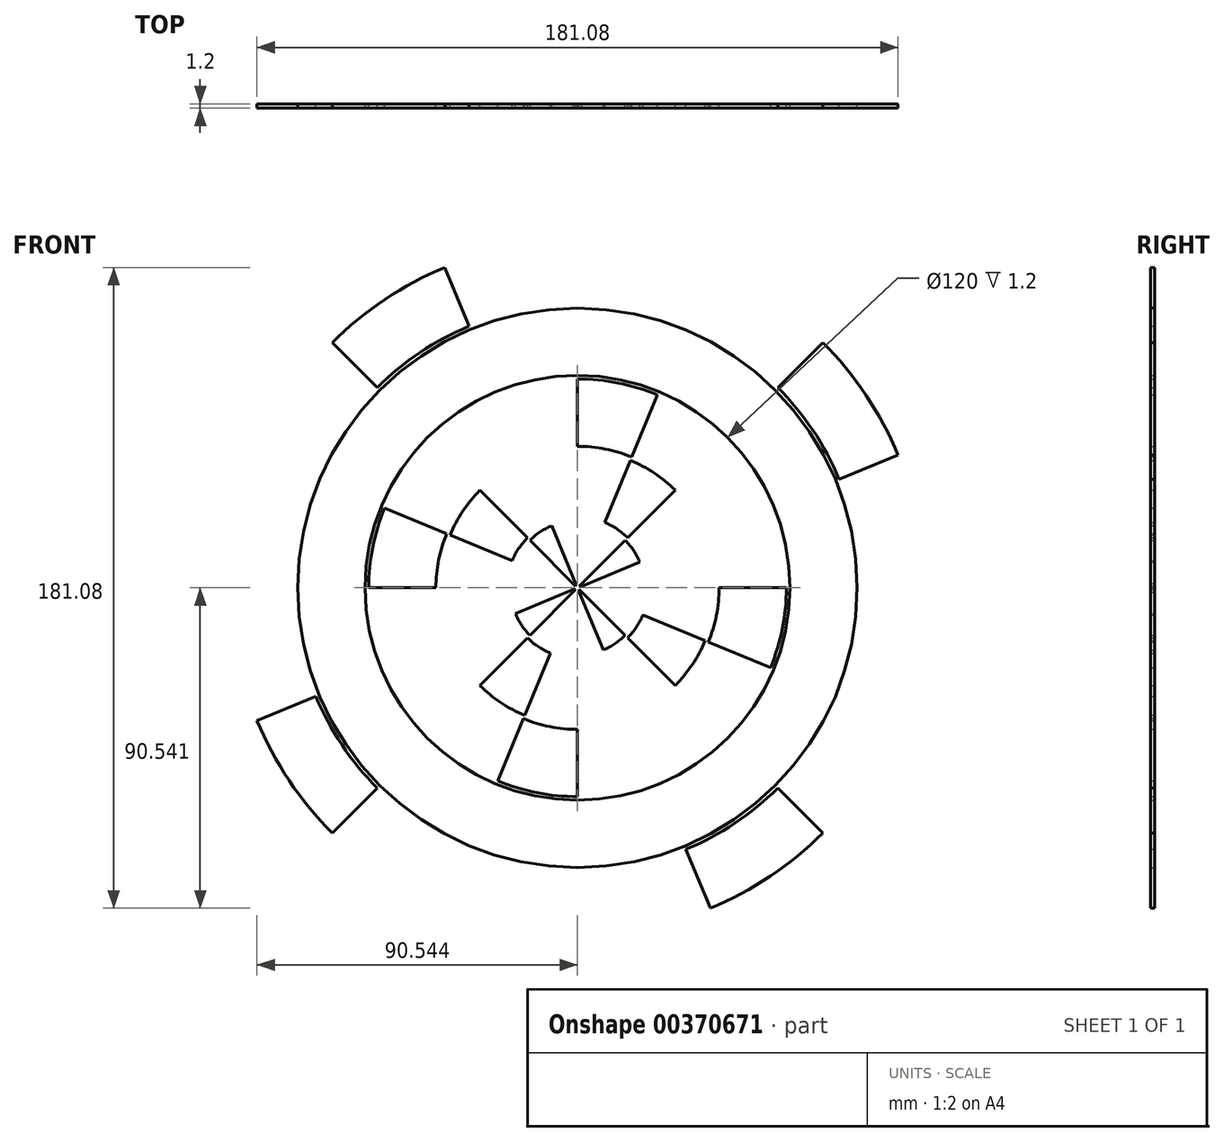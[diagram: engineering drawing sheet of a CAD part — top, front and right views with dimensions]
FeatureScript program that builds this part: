
annotation { "Feature Type Name" : "Feature", "Feature Type Description" : "" }
export const myFeature = defineFeature(function(context is Context, id is Id, definition is map)
    precondition{}
    {
        {
            var Q0;
            Q0=qCreatedBy(makeId("Front.planeOp"),FACE);
            var sketch = newSketch(context, id + "F0", { "sketchPlane" : qUnion([Q0])});
            skCircle(sketch, "E0", {"center": v(-2.5, -0.5) * mm, "radius": 80 * mm});
            skCircle(sketch, "E1", {"center": v(-2.5, -0.5) * mm, "radius": 100 * mm});
            skCircle(sketch, "E2", {"center": v(-2.5, -0.5) * mm, "radius": 60 * mm});
            skCircle(sketch, "E3", {"center": v(-2.5, -0.5) * mm, "radius": 40 * mm});
            skCircle(sketch, "E4", {"center": v(-2.5, -0.5) * mm, "radius": 20 * mm});
            skLineSegment(sketch, "E5", {"start": v(-2.5, 99.5) * mm, "end": v(-2.5, -100.5) * mm});
            skCircle(sketch, "E6", {"center": v(-2.5, -0.5) * mm, "radius": 19 * mm});
            skCircle(sketch, "E7", {"center": v(-2.5, -0.5) * mm, "radius": 39 * mm});
            skCircle(sketch, "E8", {"center": v(-2.5, -0.5) * mm, "radius": 59 * mm});
            skCircle(sketch, "E9", {"center": v(-2.5, -0.5) * mm, "radius": 79 * mm});
            skCircle(sketch, "E10", {"center": v(-2.5, -0.5) * mm, "radius": 98 * mm});
            skLineSegment(sketch, "E11.bottom", {"start": v(-21.5, 0) * mm, "end": v(16.49, 0) * mm});
            skLineSegment(sketch, "E11.top", {"start": v(-21.5, -1) * mm, "end": v(16.49, -1) * mm});
            skLineSegment(sketch, "E11.left", {"start": v(-21.5, 0) * mm, "end": v(-21.5, -1) * mm});
            skLineSegment(sketch, "E11.right", {"start": v(16.49, 0) * mm, "end": v(16.49, -1) * mm});
            skLineSegment(sketch, "E12.bottom", {"start": v(-3, 18.5) * mm, "end": v(-2, 18.5) * mm});
            skLineSegment(sketch, "E12.top", {"start": v(-3, -19.5) * mm, "end": v(-2, -19.5) * mm});
            skLineSegment(sketch, "E12.left", {"start": v(-3, 18.5) * mm, "end": v(-3, -19.5) * mm});
            skLineSegment(sketch, "E12.right", {"start": v(-2, 18.5) * mm, "end": v(-2, -19.5) * mm});
            skLineSegment(sketch, "E13", {"start": v(-2.5, -0.5) * mm, "end": v(96.5, -0.5) * mm});
            skLineSegment(sketch, "E14.1.0", {"start": v(-2.5, -0.5) * mm, "end": v(88.96, -38.38) * mm});
            skLineSegment(sketch, "E14.2.0", {"start": v(-2.5, -0.5) * mm, "end": v(67.5, -70.5) * mm});
            skLineSegment(sketch, "E14.3.0", {"start": v(-2.5, -0.5) * mm, "end": v(35.38, -91.96) * mm});
            skLineSegment(sketch, "E14.4.0", {"start": v(-2.5, -0.5) * mm, "end": v(-2.5, -99.5) * mm});
            skLineSegment(sketch, "E14.5.0", {"start": v(-2.5, -0.5) * mm, "end": v(-40.4, -91.96) * mm});
            skLineSegment(sketch, "E14.6.0", {"start": v(-2.5, -0.5) * mm, "end": v(-72.5, -70.5) * mm});
            skLineSegment(sketch, "E14.7.0", {"start": v(-2.5, -0.5) * mm, "end": v(-93.97, -38.38) * mm});
            skLineSegment(sketch, "E14.8.0", {"start": v(-2.5, -0.5) * mm, "end": v(-101.5, -0.5) * mm});
            skLineSegment(sketch, "E14.9.0", {"start": v(-2.5, -0.5) * mm, "end": v(-93.97, 37.39) * mm});
            skLineSegment(sketch, "E14.10.0", {"start": v(-2.5, -0.5) * mm, "end": v(-72.5, 69.5) * mm});
            skLineSegment(sketch, "E14.11.0", {"start": v(-2.5, -0.5) * mm, "end": v(-40.4, 90.97) * mm});
            skLineSegment(sketch, "E14.12.0", {"start": v(-2.5, -0.5) * mm, "end": v(-2.5, 98.5) * mm});
            skLineSegment(sketch, "E14.13.0", {"start": v(-2.5, -0.5) * mm, "end": v(35.38, 90.97) * mm});
            skLineSegment(sketch, "E14.14.0", {"start": v(-2.5, -0.5) * mm, "end": v(67.5, 69.5) * mm});
            skLineSegment(sketch, "E14.15.0", {"start": v(-2.5, -0.5) * mm, "end": v(88.96, 37.39) * mm});
            skLineSegment(sketch, "E14.anchor1", {"start": v(-2.5, -0.5) * mm, "end": v(96.5, -0.5) * mm, "construction": true});
            skLineSegment(sketch, "E14.anchor2", {"start": v(-2.5, -0.5) * mm, "end": v(88.96, 37.39) * mm, "construction": true});
            skSolve(sketch);
        }
        {
            var Q0;
            {var subQ0=sQuery(id+"F0.wireOp",EDGE,"E14.15.0");var subQ1=sQuery(id+"F0.wireOp",EDGE,"E6");var subQ2=makeQuery(id+"F0.imprint","INTERSECT",VERTEX,{"derivedFrom":[subQ1,subQ0]});Q0=makeQuery(id+"F0.imprint","IMPRINT",FACE,{"disambiguationData":[TD([[makeQuery(id+"F0.imprint","IMPRINT",EDGE,{"disambiguationData":[TD([[subQ2,-1.0]])],"derivedFrom":subQ1}),1.0]])]});}
            var Q1;
            {var subQ0=sQuery(id+"F0.wireOp",EDGE,"E14.14.0");var subQ1=sQuery(id+"F0.wireOp",EDGE,"E4");var subQ2=makeQuery(id+"F0.imprint","INTERSECT",VERTEX,{"derivedFrom":[subQ1,subQ0]});Q1=makeQuery(id+"F0.imprint","IMPRINT",FACE,{"disambiguationData":[TD([[makeQuery(id+"F0.imprint","IMPRINT",EDGE,{"disambiguationData":[TD([[subQ2,-1.0]])],"derivedFrom":subQ1}),-1.0]])]});}
            var Q2;
            {var subQ0=sQuery(id+"F0.wireOp",EDGE,"E14.13.0");var subQ1=sQuery(id+"F0.wireOp",EDGE,"E3");var subQ2=makeQuery(id+"F0.imprint","INTERSECT",VERTEX,{"derivedFrom":[subQ1,subQ0]});Q2=makeQuery(id+"F0.imprint","IMPRINT",FACE,{"disambiguationData":[TD([[makeQuery(id+"F0.imprint","IMPRINT",EDGE,{"disambiguationData":[TD([[subQ2,-1.0]])],"derivedFrom":subQ1}),-1.0]])]});}
            var Q3;
            {var subQ0=sQuery(id+"F0.wireOp",EDGE,"E14.12.0");var subQ1=sQuery(id+"F0.wireOp",EDGE,"E2");var subQ2=makeQuery(id+"F0.imprint","INTERSECT",VERTEX,{"derivedFrom":[subQ1,subQ0]});Q3=makeQuery(id+"F0.imprint","IMPRINT",FACE,{"disambiguationData":[TD([[makeQuery(id+"F0.imprint","IMPRINT",EDGE,{"disambiguationData":[TD([[subQ2,-1.0]])],"derivedFrom":subQ1}),-1.0]])]});}
            var Q4;
            {var subQ0=sQuery(id+"F0.wireOp",EDGE,"E14.11.0");var subQ1=sQuery(id+"F0.wireOp",EDGE,"E0");var subQ2=makeQuery(id+"F0.imprint","INTERSECT",VERTEX,{"derivedFrom":[subQ1,subQ0]});Q4=makeQuery(id+"F0.imprint","IMPRINT",FACE,{"disambiguationData":[TD([[makeQuery(id+"F0.imprint","IMPRINT",EDGE,{"disambiguationData":[TD([[subQ2,-1.0]])],"derivedFrom":subQ1}),-1.0]])]});}
            var Q5;
            {var subQ0=sQuery(id+"F0.wireOp",EDGE,"E14.11.0");var subQ1=sQuery(id+"F0.wireOp",EDGE,"E6");var subQ2=makeQuery(id+"F0.imprint","INTERSECT",VERTEX,{"derivedFrom":[subQ1,subQ0]});Q5=makeQuery(id+"F0.imprint","IMPRINT",FACE,{"disambiguationData":[TD([[makeQuery(id+"F0.imprint","IMPRINT",EDGE,{"disambiguationData":[TD([[subQ2,-1.0]])],"derivedFrom":subQ1}),1.0]])]});}
            var Q6;
            {var subQ0=sQuery(id+"F0.wireOp",EDGE,"E14.10.0");var subQ1=sQuery(id+"F0.wireOp",EDGE,"E4");var subQ2=makeQuery(id+"F0.imprint","INTERSECT",VERTEX,{"derivedFrom":[subQ1,subQ0]});Q6=makeQuery(id+"F0.imprint","IMPRINT",FACE,{"disambiguationData":[TD([[makeQuery(id+"F0.imprint","IMPRINT",EDGE,{"disambiguationData":[TD([[subQ2,-1.0]])],"derivedFrom":subQ1}),-1.0]])]});}
            var Q7;
            {var subQ0=sQuery(id+"F0.wireOp",EDGE,"E14.9.0");var subQ1=sQuery(id+"F0.wireOp",EDGE,"E3");var subQ2=makeQuery(id+"F0.imprint","INTERSECT",VERTEX,{"derivedFrom":[subQ1,subQ0]});Q7=makeQuery(id+"F0.imprint","IMPRINT",FACE,{"disambiguationData":[TD([[makeQuery(id+"F0.imprint","IMPRINT",EDGE,{"disambiguationData":[TD([[subQ2,-1.0]])],"derivedFrom":subQ1}),-1.0]])]});}
            var Q8;
            {var subQ0=sQuery(id+"F0.wireOp",EDGE,"E14.8.0");var subQ1=sQuery(id+"F0.wireOp",EDGE,"E2");var subQ2=makeQuery(id+"F0.imprint","INTERSECT",VERTEX,{"derivedFrom":[subQ1,subQ0]});Q8=makeQuery(id+"F0.imprint","IMPRINT",FACE,{"disambiguationData":[TD([[makeQuery(id+"F0.imprint","IMPRINT",EDGE,{"disambiguationData":[TD([[subQ2,-1.0]])],"derivedFrom":subQ1}),-1.0]])]});}
            var Q9;
            {var subQ0=sQuery(id+"F0.wireOp",EDGE,"E14.7.0");var subQ1=sQuery(id+"F0.wireOp",EDGE,"E0");var subQ2=makeQuery(id+"F0.imprint","INTERSECT",VERTEX,{"derivedFrom":[subQ1,subQ0]});Q9=makeQuery(id+"F0.imprint","IMPRINT",FACE,{"disambiguationData":[TD([[makeQuery(id+"F0.imprint","IMPRINT",EDGE,{"disambiguationData":[TD([[subQ2,-1.0]])],"derivedFrom":subQ1}),-1.0]])]});}
            var Q10;
            {var subQ0=sQuery(id+"F0.wireOp",EDGE,"E14.7.0");var subQ1=sQuery(id+"F0.wireOp",EDGE,"E6");var subQ2=makeQuery(id+"F0.imprint","INTERSECT",VERTEX,{"derivedFrom":[subQ1,subQ0]});Q10=makeQuery(id+"F0.imprint","IMPRINT",FACE,{"disambiguationData":[TD([[makeQuery(id+"F0.imprint","IMPRINT",EDGE,{"disambiguationData":[TD([[subQ2,-1.0]])],"derivedFrom":subQ1}),1.0]])]});}
            var Q11;
            {var subQ0=sQuery(id+"F0.wireOp",EDGE,"E14.6.0");var subQ1=sQuery(id+"F0.wireOp",EDGE,"E4");var subQ2=makeQuery(id+"F0.imprint","INTERSECT",VERTEX,{"derivedFrom":[subQ1,subQ0]});Q11=makeQuery(id+"F0.imprint","IMPRINT",FACE,{"disambiguationData":[TD([[makeQuery(id+"F0.imprint","IMPRINT",EDGE,{"disambiguationData":[TD([[subQ2,-1.0]])],"derivedFrom":subQ1}),-1.0]])]});}
            var Q12;
            {var subQ0=sQuery(id+"F0.wireOp",EDGE,"E14.5.0");var subQ1=sQuery(id+"F0.wireOp",EDGE,"E3");var subQ2=makeQuery(id+"F0.imprint","INTERSECT",VERTEX,{"derivedFrom":[subQ1,subQ0]});Q12=makeQuery(id+"F0.imprint","IMPRINT",FACE,{"disambiguationData":[TD([[makeQuery(id+"F0.imprint","IMPRINT",EDGE,{"disambiguationData":[TD([[subQ2,-1.0]])],"derivedFrom":subQ1}),-1.0]])]});}
            var Q13;
            {var subQ0=sQuery(id+"F0.wireOp",EDGE,"E14.4.0");var subQ1=sQuery(id+"F0.wireOp",EDGE,"E2");var subQ2=makeQuery(id+"F0.imprint","INTERSECT",VERTEX,{"derivedFrom":[subQ1,subQ0]});Q13=makeQuery(id+"F0.imprint","IMPRINT",FACE,{"disambiguationData":[TD([[makeQuery(id+"F0.imprint","IMPRINT",EDGE,{"disambiguationData":[TD([[subQ2,-1.0]])],"derivedFrom":subQ1}),-1.0]])]});}
            var Q14;
            {var subQ0=sQuery(id+"F0.wireOp",EDGE,"E14.3.0");var subQ1=sQuery(id+"F0.wireOp",EDGE,"E0");var subQ2=makeQuery(id+"F0.imprint","INTERSECT",VERTEX,{"derivedFrom":[subQ1,subQ0]});Q14=makeQuery(id+"F0.imprint","IMPRINT",FACE,{"disambiguationData":[TD([[makeQuery(id+"F0.imprint","IMPRINT",EDGE,{"disambiguationData":[TD([[subQ2,-1.0]])],"derivedFrom":subQ1}),-1.0]])]});}
            var Q15;
            {var subQ0=sQuery(id+"F0.wireOp",EDGE,"E14.3.0");var subQ1=sQuery(id+"F0.wireOp",EDGE,"E6");var subQ2=makeQuery(id+"F0.imprint","INTERSECT",VERTEX,{"derivedFrom":[subQ1,subQ0]});Q15=makeQuery(id+"F0.imprint","IMPRINT",FACE,{"disambiguationData":[TD([[makeQuery(id+"F0.imprint","IMPRINT",EDGE,{"disambiguationData":[TD([[subQ2,-1.0]])],"derivedFrom":subQ1}),1.0]])]});}
            var Q16;
            {var subQ0=sQuery(id+"F0.wireOp",EDGE,"E14.2.0");var subQ1=sQuery(id+"F0.wireOp",EDGE,"E4");var subQ2=makeQuery(id+"F0.imprint","INTERSECT",VERTEX,{"derivedFrom":[subQ1,subQ0]});Q16=makeQuery(id+"F0.imprint","IMPRINT",FACE,{"disambiguationData":[TD([[makeQuery(id+"F0.imprint","IMPRINT",EDGE,{"disambiguationData":[TD([[subQ2,-1.0]])],"derivedFrom":subQ1}),-1.0]])]});}
            var Q17;
            {var subQ0=sQuery(id+"F0.wireOp",EDGE,"E13");var subQ1=sQuery(id+"F0.wireOp",EDGE,"E3");var subQ2=makeQuery(id+"F0.imprint","INTERSECT",VERTEX,{"derivedFrom":[subQ1,subQ0]});Q17=makeQuery(id+"F0.imprint","IMPRINT",FACE,{"disambiguationData":[TD([[makeQuery(id+"F0.imprint","IMPRINT",EDGE,{"disambiguationData":[TD([[subQ2,1.0]])],"derivedFrom":subQ1}),-1.0]])]});}
            var Q18;
            {var subQ0=sQuery(id+"F0.wireOp",EDGE,"E14.15.0");var subQ1=sQuery(id+"F0.wireOp",EDGE,"E2");var subQ2=makeQuery(id+"F0.imprint","INTERSECT",VERTEX,{"derivedFrom":[subQ1,subQ0]});Q18=makeQuery(id+"F0.imprint","IMPRINT",FACE,{"disambiguationData":[TD([[makeQuery(id+"F0.imprint","IMPRINT",EDGE,{"disambiguationData":[TD([[subQ2,1.0]])],"derivedFrom":subQ1}),-1.0]])]});}
            var Q19;
            {var subQ0=sQuery(id+"F0.wireOp",EDGE,"E14.15.0");var subQ1=sQuery(id+"F0.wireOp",EDGE,"E0");var subQ2=makeQuery(id+"F0.imprint","INTERSECT",VERTEX,{"derivedFrom":[subQ1,subQ0]});Q19=makeQuery(id+"F0.imprint","IMPRINT",FACE,{"disambiguationData":[TD([[makeQuery(id+"F0.imprint","IMPRINT",EDGE,{"disambiguationData":[TD([[subQ2,-1.0]])],"derivedFrom":subQ1}),-1.0]])]});}
            extrude(context, id + "F1", {"entities" : qUnion([Q0, Q1, Q2, Q3, Q4, Q5, Q6, Q7, Q8, Q9, Q10, Q11, Q12, Q13, Q14, Q15, Q16, Q17, Q18, Q19]), "depth" : 1.2 * mm});
        }
    });
